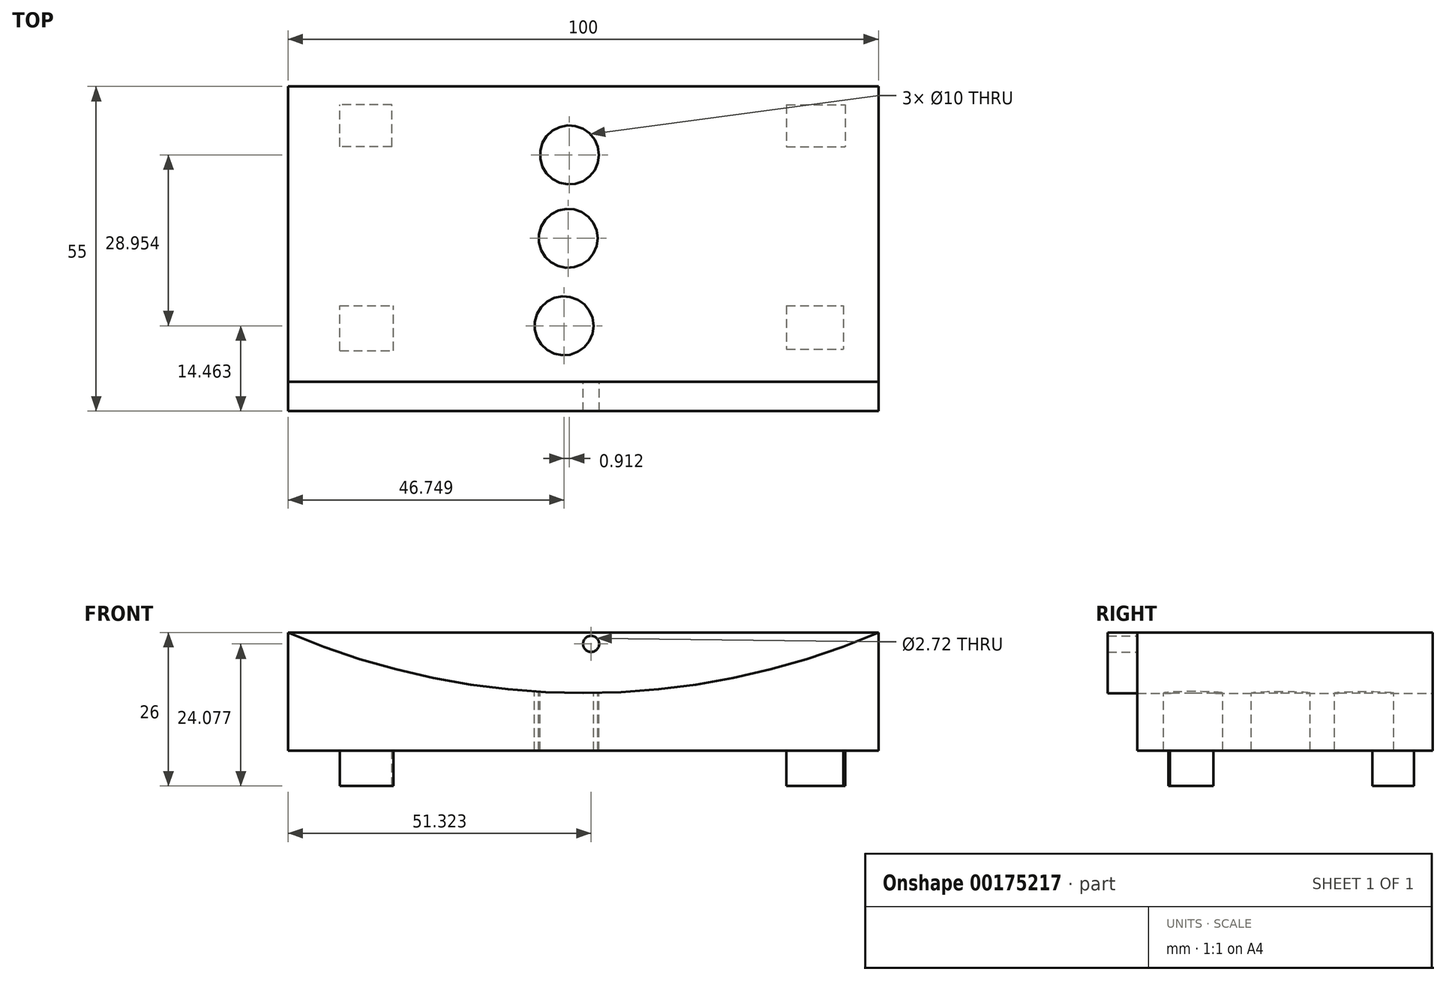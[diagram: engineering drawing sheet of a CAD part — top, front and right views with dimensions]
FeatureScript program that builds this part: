
annotation { "Feature Type Name" : "Feature", "Feature Type Description" : "" }
export const myFeature = defineFeature(function(context is Context, id is Id, definition is map)
    precondition{}
    {
        {
            var Q0;
            Q0=qCreatedBy(makeId("Front.planeOp"),FACE);
            var sketch = newSketch(context, id + "F0", { "sketchPlane" : qUnion([Q0])});
            skLineSegment(sketch, "E0", {"start": v(-40.8, 0) * mm, "end": v(-40.8, 20) * mm});
            skLineSegment(sketch, "E1", {"start": v(-40.8, 0) * mm, "end": v(59.2, 0) * mm});
            skLineSegment(sketch, "E2", {"start": v(59.2, 0) * mm, "end": v(59.2, 20) * mm});
            skArc(sketch, "E3", {"start": v(-40.8, 20) * mm, "mid": v(9.2, 9.74) * mm, "end": v(59.2, 20) * mm});
            skSolve(sketch);
        }
        {
            var Q0;
            Q0=makeQuery(id+"F0.imprint","IMPRINT",FACE,{"disambiguationData":[TD([[makeQuery(id+"F0.imprint","IMPRINT",EDGE,{"derivedFrom":sQuery(id+"F0.wireOp",EDGE,"E0")}),-1.0]])]});
            extrude(context, id + "F1", {"entities" : qUnion([Q0]), "depth" : 50 * mm});
        }
        {
            var Q0;
            Q0=qCreatedBy(makeId("Top.planeOp"),FACE);
            var sketch = newSketch(context, id + "F2", { "sketchPlane" : qUnion([Q0])});
            skCircle(sketch, "E4", {"center": v(6.86, -11.58) * mm, "radius": 5 * mm});
            skCircle(sketch, "E5", {"center": v(6.63, -25.72) * mm, "radius": 5 * mm});
            skCircle(sketch, "E6", {"center": v(5.95, -40.54) * mm, "radius": 5 * mm});
            skSolve(sketch);
        }
        {
            var Q0;
            Q0 = qSketchRegion(id + "F2", true);
            extrude(context, id + "F3", {"entities" : qUnion([Q0]), "operationType" : NewBodyOperationType.ADD, "depth" : 25 * mm});
        }
        {
            var Q0;
            Q0 = qSketchRegion(id + "F2", true);
            var Q1;
            Q1=makeQuery(id+"F3.opExtrude","CAP_FACE",FACE,{"disambiguationData":[OSD([sQuery(id+"F2.wireOp",EDGE,"E5")])],"isStart":false});
            var Q2;
            Q2=makeQuery(id+"F3.opExtrude","CAP_FACE",FACE,{"disambiguationData":[OSD([sQuery(id+"F2.wireOp",EDGE,"E6")])],"isStart":false});
            extrude(context, id + "F4", {"entities" : qUnion([Q0, Q1, Q2]), "operationType" : NewBodyOperationType.REMOVE, "endBound" : BoundingType.THROUGH_ALL, "oppositeDirection" : true, "depth" : 25 * mm});
        }
        {
            var Q0;
            Q0=makeQuery(id+"F3.opExtrude","CAP_FACE",FACE,{"disambiguationData":[OSD([sQuery(id+"F2.wireOp",EDGE,"E4")])],"isStart":false});
            extrude(context, id + "F5", {"entities" : qUnion([Q0]), "operationType" : NewBodyOperationType.REMOVE, "endBound" : BoundingType.THROUGH_ALL, "oppositeDirection" : true, "depth" : 25 * mm});
        }
        {
            var Q0;
            Q0=qCreatedBy(makeId("Top.planeOp"),FACE);
            var sketch = newSketch(context, id + "F6", { "sketchPlane" : qUnion([Q0])});
            skLineSegment(sketch, "E7.bottom", {"start": v(-30.31, -58.35) * mm, "end": v(-23.23, -58.35) * mm});
            skLineSegment(sketch, "E7.top", {"start": v(-30.31, -52.4) * mm, "end": v(-23.23, -52.4) * mm});
            skLineSegment(sketch, "E7.left", {"start": v(-30.31, -58.35) * mm, "end": v(-30.31, -52.4) * mm});
            skLineSegment(sketch, "E7.right", {"start": v(-23.23, -58.35) * mm, "end": v(-23.23, -52.4) * mm});
            skLineSegment(sketch, "E8.bottom", {"start": v(-23.23, -10.2) * mm, "end": v(-32, -10.2) * mm});
            skLineSegment(sketch, "E8.top", {"start": v(-23.23, -3.12) * mm, "end": v(-32, -3.12) * mm});
            skLineSegment(sketch, "E8.left", {"start": v(-23.23, -10.2) * mm, "end": v(-23.23, -3.12) * mm});
            skLineSegment(sketch, "E8.right", {"start": v(-32, -10.2) * mm, "end": v(-32, -3.12) * mm});
            skPoint(sketch, "E9.oppositeSnap0", {"position": v(-27.62, -10.2) * mm});
            skLineSegment(sketch, "E9.bottom", {"start": v(43.62, -3.12) * mm, "end": v(53.54, -3.12) * mm});
            skLineSegment(sketch, "E9.top", {"start": v(43.62, -10.2) * mm, "end": v(53.54, -10.2) * mm});
            skLineSegment(sketch, "E9.left", {"start": v(43.62, -3.12) * mm, "end": v(43.62, -10.2) * mm});
            skLineSegment(sketch, "E9.right", {"start": v(53.54, -3.12) * mm, "end": v(53.54, -10.2) * mm});
            skLineSegment(sketch, "E10.bottom", {"start": v(43.62, -52.4) * mm, "end": v(53.54, -52.4) * mm});
            skLineSegment(sketch, "E10.top", {"start": v(43.62, -58.35) * mm, "end": v(53.54, -58.35) * mm});
            skLineSegment(sketch, "E10.left", {"start": v(43.62, -52.4) * mm, "end": v(43.62, -58.35) * mm});
            skLineSegment(sketch, "E10.right", {"start": v(53.54, -52.4) * mm, "end": v(53.54, -58.35) * mm});
            skSolve(sketch);
        }
        {
            var Q0;
            Q0=makeQuery(id+"F6.imprint","IMPRINT",FACE,{"disambiguationData":[TD([[makeQuery(id+"F6.imprint","IMPRINT",EDGE,{"derivedFrom":sQuery(id+"F6.wireOp",EDGE,"E7.bottom")}),1.0]])]});
            var Q1;
            Q1=makeQuery(id+"F6.imprint","IMPRINT",FACE,{"disambiguationData":[TD([[makeQuery(id+"F6.imprint","IMPRINT",EDGE,{"derivedFrom":sQuery(id+"F6.wireOp",EDGE,"E10.bottom")}),-1.0]])]});
            var Q2;
            Q2=makeQuery(id+"F6.imprint","IMPRINT",FACE,{"disambiguationData":[TD([[makeQuery(id+"F6.imprint","IMPRINT",EDGE,{"derivedFrom":sQuery(id+"F6.wireOp",EDGE,"E9.bottom")}),-1.0]])]});
            var Q3;
            Q3=makeQuery(id+"F6.imprint","IMPRINT",FACE,{"disambiguationData":[TD([[makeQuery(id+"F6.imprint","IMPRINT",EDGE,{"derivedFrom":sQuery(id+"F6.wireOp",EDGE,"E8.bottom")}),-1.0]])]});
            extrude(context, id + "F7", {"entities" : qUnion([Q0, Q1, Q2, Q3]), "operationType" : NewBodyOperationType.ADD, "oppositeDirection" : true, "depth" : 6 * mm});
        }
        {
            var Q0;
            Q0=makeQuery(id+"F7.opExtrude","SWEPT_BODY",BODY,{"disambiguationData":[OSD([sQuery(id+"F6.wireOp",EDGE,"E10.bottom"),sQuery(id+"F6.wireOp",EDGE,"E10.top"),sQuery(id+"F6.wireOp",EDGE,"E10.left"),sQuery(id+"F6.wireOp",EDGE,"E10.right")])]});
            deleteBodies(context, id + "F8", {"entities" : qUnion([Q0])});
        }
        {
            var Q0;
            Q0=makeQuery(id+"F7.opExtrude","SWEPT_BODY",BODY,{"disambiguationData":[OSD([sQuery(id+"F6.wireOp",EDGE,"E7.bottom"),sQuery(id+"F6.wireOp",EDGE,"E7.top"),sQuery(id+"F6.wireOp",EDGE,"E7.left"),sQuery(id+"F6.wireOp",EDGE,"E7.right")])]});
            deleteBodies(context, id + "F9", {"entities" : qUnion([Q0])});
        }
        {
            var Q0;
            Q0=makeQuery(id+"F1.opExtrude","CAP_FACE",FACE,{"disambiguationData":[OSD([sQuery(id+"F0.wireOp",EDGE,"E0"),sQuery(id+"F0.wireOp",EDGE,"E1"),sQuery(id+"F0.wireOp",EDGE,"E2"),sQuery(id+"F0.wireOp",EDGE,"E3")])],"isStart":false});
            var sketch = newSketch(context, id + "F10", { "sketchPlane" : qUnion([Q0])});
            skLineSegment(sketch, "E11", {"start": v(-40.8, 20) * mm, "end": v(59.2, 20) * mm});
            skSolve(sketch);
        }
        {
            var Q0;
            Q0=makeQuery(id+"F10.imprint","IMPRINT",FACE,{"disambiguationData":[TD([[makeQuery(id+"F10.imprint","IMPRINT",EDGE,{"derivedFrom":sQuery(id+"F10.wireOp",EDGE,"E11")}),-1.0]])]});
            extrude(context, id + "F11", {"entities" : qUnion([Q0]), "depth" : 5 * mm});
        }
        {
            var Q0;
            Q0=qCreatedBy(makeId("Front.planeOp"),FACE);
            var sketch = newSketch(context, id + "F12", { "sketchPlane" : qUnion([Q0])});
            skCircle(sketch, "E12", {"center": v(3.9, 17.78) * mm, "radius": 1.24 * mm});
            skSolve(sketch);
        }
        {
            var Q0;
            Q0=makeQuery(id+"F12.imprint","IMPRINT",FACE,{"disambiguationData":[TD([[makeQuery(id+"F12.imprint","IMPRINT",EDGE,{"derivedFrom":sQuery(id+"F12.wireOp",EDGE,"E12")}),1.0]])]});
            extrude(context, id + "F13", {"entities" : qUnion([Q0]), "operationType" : NewBodyOperationType.REMOVE, "endBound" : BoundingType.THROUGH_ALL, "oppositeDirection" : true, "depth" : 25 * mm});
        }
        {
            var Q0;
            Q0=makeQuery(id+"F11.opExtrude","CAP_FACE",FACE,{"disambiguationData":[OSD([sQuery(id+"F0.wireOp",EDGE,"E3"),sQuery(id+"F10.wireOp",EDGE,"E11")])],"isStart":true});
            var sketch = newSketch(context, id + "F14", { "sketchPlane" : qUnion([Q0])});
            skCircle(sketch, "E13", {"center": v(-10.52, 18.08) * mm, "radius": 1.36 * mm});
            skSolve(sketch);
        }
        {
            var Q0;
            Q0 = qSketchRegion(id + "F14", true);
            extrude(context, id + "F15", {"entities" : qUnion([Q0]), "operationType" : NewBodyOperationType.REMOVE, "oppositeDirection" : true, "depth" : 33.4 * mm});
        }
        {
            var Q0;
            Q0=makeQuery(id+"F1.opExtrude","SWEPT_FACE",FACE,{"disambiguationData":[OSD([sQuery(id+"F0.wireOp",EDGE,"E1")])]});
            var sketch = newSketch(context, id + "F16", { "sketchPlane" : qUnion([Q0])});
            skLineSegment(sketch, "E14.bottom", {"start": v(-32, 44.76) * mm, "end": v(-22.95, 44.76) * mm});
            skLineSegment(sketch, "E14.top", {"start": v(-32, 37.1) * mm, "end": v(-22.95, 37.1) * mm});
            skLineSegment(sketch, "E14.left", {"start": v(-32, 44.76) * mm, "end": v(-32, 37.1) * mm});
            skLineSegment(sketch, "E14.right", {"start": v(-22.95, 44.76) * mm, "end": v(-22.95, 37.1) * mm});
            skLineSegment(sketch, "E15.bottom", {"start": v(43.62, 10.2) * mm, "end": v(43.62, 10.2) * mm});
            skLineSegment(sketch, "E15.top", {"start": v(43.62, 37.1) * mm, "end": v(43.62, 37.1) * mm});
            skLineSegment(sketch, "E16.bottom", {"start": v(43.62, 37.1) * mm, "end": v(53.26, 37.1) * mm});
            skLineSegment(sketch, "E16.top", {"start": v(43.62, 44.47) * mm, "end": v(53.26, 44.47) * mm});
            skLineSegment(sketch, "E16.left", {"start": v(43.62, 37.1) * mm, "end": v(43.62, 44.47) * mm});
            skLineSegment(sketch, "E16.right", {"start": v(53.26, 37.1) * mm, "end": v(53.26, 44.47) * mm});
            skSolve(sketch);
        }
        {
            var Q0;
            Q0 = qSketchRegion(id + "F16", true);
            extrude(context, id + "F17", {"entities" : qUnion([Q0]), "operationType" : NewBodyOperationType.ADD, "depth" : 6 * mm});
        }
    });
